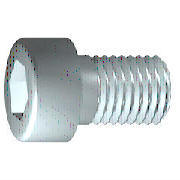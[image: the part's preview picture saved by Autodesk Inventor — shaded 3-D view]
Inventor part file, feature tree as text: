
AUTODESK INVENTOR PART (.ipt)
format: ipt  version: 2020 (Build 240168000, 168)  size: 187,392 bytes
history: native  units: mm (DEFAULTED — no unit token found)
features: sketch x2, extrude x1, plane x1, fillet x1
ambient origin geometry x7: Origin, YZ Plane, XY Plane, X Axis, Y Axis, Z Axis, Center Point
bodies: Solid1 (feature_tree), Body (feature_tree)
feature tree (5):
  extrude  "Slot"  Depth=5.0mm
  plane  "Work Plane1"
  fillet  "Fillet2"  Radius=5.0mm
  sketch  "Sketch1"  dims[d1=22.0mm d2=0.766912mm d3=5.0mm]
  sketch  "Sketch2"  dims[d4=3.8mm d5=60.0deg d6=8.0mm d7=8.0mm d8=5.773503mm d9=13.0mm d10=90.0deg d11=10.0mm d12=0.0mm d13=22.0mm d14=0.0mm d15=0.766813mm d16=0.766813mm d17=0.8mm d19=0.0mm d26=80.0mm d27=45.0deg d28=0.0mm d29=0.0mm d30=0.1mm]
